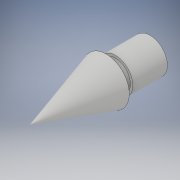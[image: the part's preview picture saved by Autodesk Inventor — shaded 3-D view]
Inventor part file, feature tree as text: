
AUTODESK INVENTOR PART (.ipt)
format: ipt  version: 2018 (Build 220112000, 112)  size: 123,392 bytes
history: native  units: in
note: dims shown in document units (in); Inventor stores cm internally (conversion verified against a paired STEP export)
features: revolve x1, sketch x1
ambient origin geometry x8: Origin, YZ Plane, XZ Plane, XY Plane, X Axis, Y Axis, Z Axis, Center Point
bodies: Solid1 (feature_tree)
feature tree (2):
  revolve  "Revolution1"  [1 undecoded]
  sketch  "Sketch1"  dims[d0=0.33in d1=0.04in d2=0.15in d3=0.1in d4=0.065in d5=0.075in d6=0.04in d7=0.01in d8=90.0deg]
note: 1 required parameter value undecoded (feature->parameter linkage not recoverable at this tier; creation-order binding heuristic only, values carry confidence <= 0.55)
